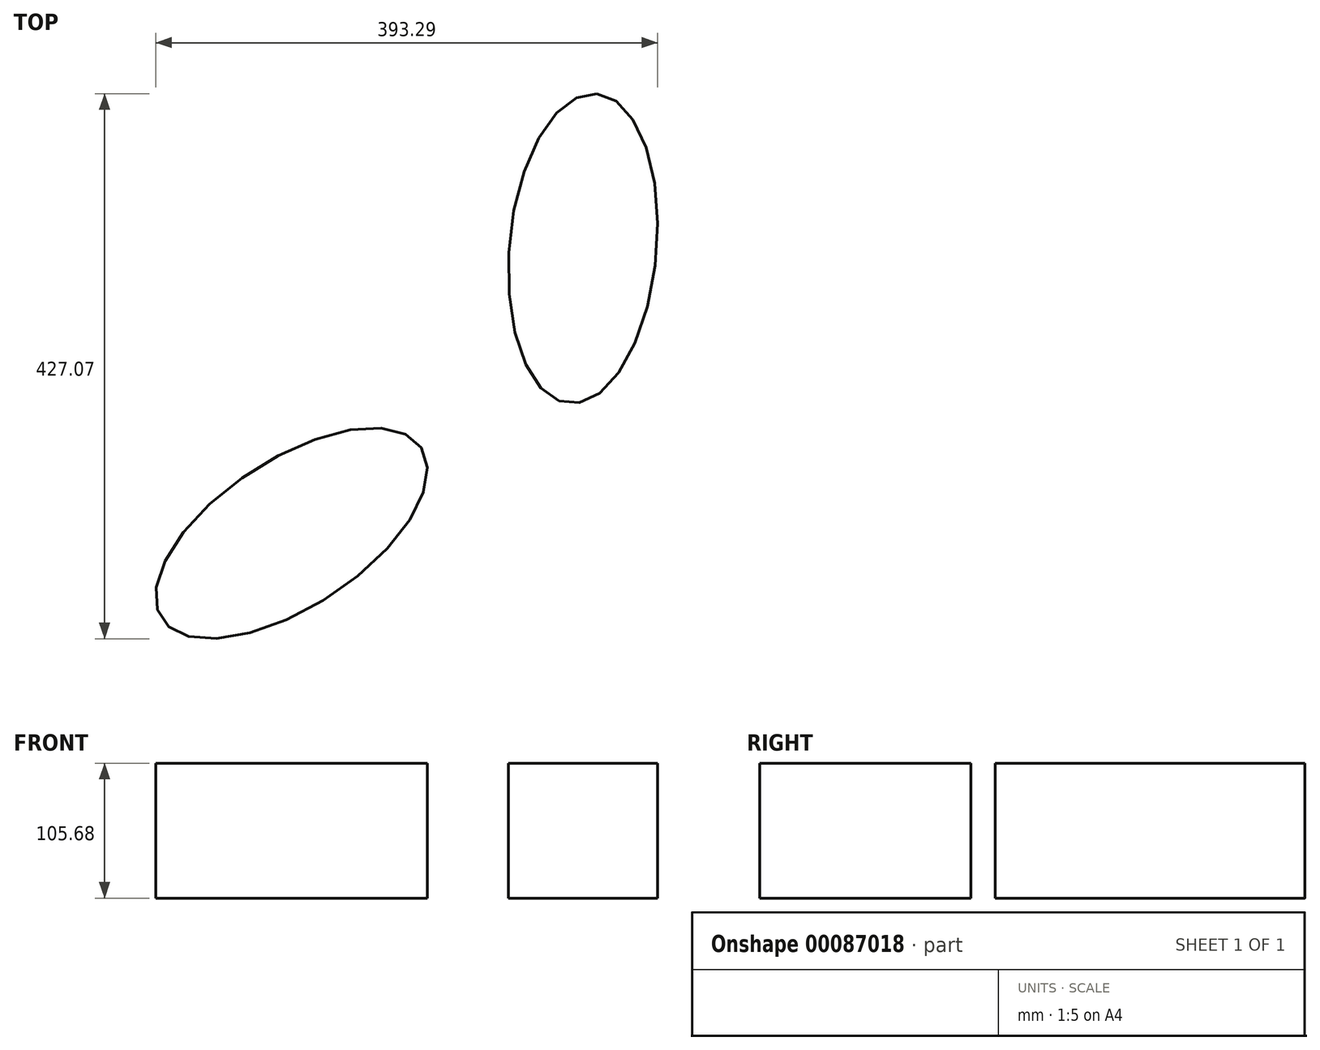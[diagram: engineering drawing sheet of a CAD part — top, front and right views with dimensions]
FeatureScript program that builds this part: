
annotation { "Feature Type Name" : "Feature", "Feature Type Description" : "" }
export const myFeature = defineFeature(function(context is Context, id is Id, definition is map)
    precondition{}
    {
        {
            var Q0;
            Q0=qCreatedBy(makeId("Top.planeOp"),FACE);
            var sketch = newSketch(context, id + "F0", { "sketchPlane" : qUnion([Q0])});
            skCircle(sketch, "E0", {"center": v(73.46, 0) * mm, "radius": 35.32 * mm});
            skCircle(sketch, "E1", {"center": v(73.46, -114.86) * mm, "radius": 11.3 * mm});
            skLineSegment(sketch, "E2", {"start": v(-153.3, -43.25) * mm, "end": v(-117, 51.28) * mm});
            skLineSegment(sketch, "E3", {"start": v(-117, 51.28) * mm, "end": v(-90.27, -12.71) * mm});
            skLineSegment(sketch, "E4", {"start": v(-90.27, -12.71) * mm, "end": v(-133.06, -53.37) * mm});
            skLineSegment(sketch, "E5", {"start": v(-182.15, -7.77) * mm, "end": v(-133.06, 50.56) * mm});
            skLineSegment(sketch, "E6.top", {"start": v(-54.52, 0) * mm, "end": v(73.46, 0) * mm});
            skLineSegment(sketch, "E6.left", {"start": v(-54.52, 24.2) * mm, "end": v(-54.52, 0) * mm});
            skLineSegment(sketch, "E7.bottom", {"start": v(131.67, -31.4) * mm, "end": v(153.76, -31.4) * mm});
            skLineSegment(sketch, "E7.top", {"start": v(131.67, -11.06) * mm, "end": v(153.76, -11.06) * mm});
            skLineSegment(sketch, "E7.left", {"start": v(131.67, -31.4) * mm, "end": v(131.67, -11.06) * mm});
            skLineSegment(sketch, "E7.right", {"start": v(153.76, -31.4) * mm, "end": v(153.76, -11.06) * mm});
            skEllipse(sketch, "E8", {"center": v(-15.34, 67.77) * mm, "majorRadius": 6.88 * mm, "minorRadius": 95.43 * mm, "majorAxis": v(-0.66, -0.75)});
            skArc(sketch, "E9", {"start": v(-139.46, -67.7) * mm, "mid": v(-100.06, -76.7) * mm, "end": v(-133.06, -53.37) * mm});
            skFitSpline(sketch, "E10", {"points": [v(101.11, -98.73) * mm, v(222.96, -90.1) * mm, v(188, -20.78) * mm, v(254.86, 0) * mm, v(125.27, 113.69) * mm, v(92, 99.58) * mm], "startDerivative": vector(706.16, -108.12) * mm, "endDerivative": vector(-179.65, -192.92) * mm, "construction": true});
            skFitSpline(sketch, "E11.0", {"points": [v(104.25, -44.37) * mm, v(108.35, -40.06) * mm, v(112.06, -35.4) * mm, v(115.31, -30.53) * mm, v(118.06, -25.54) * mm, v(120.3, -20.56) * mm, v(122.06, -15.7) * mm, v(123.38, -11) * mm, v(124.3, -6.56) * mm, v(125.1, -1) * mm, v(125.42, 5.23) * mm, v(125.13, 11.56) * mm, v(124.44, 16.87) * mm, v(123.54, 21.34) * mm, v(122.55, 25.12) * mm, v(121.52, 28.34) * mm, v(120.51, 31.11) * mm, v(119.2, 34.32) * mm, v(117.66, 37.58) * mm, v(116, 40.72) * mm, v(114.47, 43.32) * mm, v(113.08, 45.53) * mm, v(111.79, 47.47) * mm, v(110.16, 49.79) * mm, v(108.27, 52.32) * mm, v(106.1, 55.05) * mm, v(103.98, 57.61) * mm, v(101.84, 60.1) * mm, v(99.65, 62.55) * mm, v(97.4, 65.02) * mm, v(95.05, 67.53) * mm, v(92.6, 70.09) * mm, v(90.06, 72.71) * mm, v(87.4, 75.4) * mm, v(84.64, 78.17) * mm, v(81.8, 80.98) * mm, v(78.86, 83.85) * mm, v(74.83, 87.73) * mm, v(69.6, 92.71) * mm, v(63, 98.87) * mm, v(56.13, 105.17) * mm, v(50.22, 110.52) * mm, v(45.38, 114.85) * mm, v(41.71, 118.1) * mm, v(38.62, 120.83) * mm, v(36.13, 123.02) * mm, v(34.25, 124.66) * mm, v(32.37, 126.3) * mm, v(29.86, 128.46) * mm, v(26.74, 131.15) * mm, v(23.01, 134.35) * mm, v(18.07, 138.55) * mm, v(11.96, 143.68) * mm, v(4.78, 149.62) * mm, v(-2.21, 155.31) * mm, v(-7.86, 159.83) * mm, v(-12.26, 163.29) * mm, v(-15.5, 165.8) * mm, v(-18.67, 168.24) * mm, v(-21.79, 170.6) * mm, v(-24.82, 172.87) * mm, v(-27.77, 175.03) * mm, v(-30.64, 177.1) * mm, v(-33.44, 179.08) * mm, v(-36.2, 180.97) * mm, v(-38.93, 182.8) * mm, v(-41.68, 184.59) * mm, v(-44.5, 186.35) * mm, v(-47.5, 188.12) * mm, v(-50.27, 189.65) * mm, v(-52.8, 190.94) * mm, v(-54.9, 191.96) * mm, v(-57.27, 193.04) * mm, v(-60.05, 194.19) * mm, v(-63.38, 195.41) * mm, v(-66.83, 196.5) * mm, v(-70.19, 197.35) * mm, v(-73.07, 197.98) * mm, v(-76.4, 198.56) * mm, v(-80.28, 199.03) * mm, v(-84.83, 199.3) * mm, v(-90.19, 199.26) * mm, v(-96.5, 198.7) * mm, v(-102.61, 197.52) * mm, v(-108.02, 195.97) * mm, v(-112.3, 194.45) * mm, v(-116.76, 192.5) * mm, v(-121.35, 190.1) * mm, v(-125.98, 187.2) * mm, v(-130.54, 183.8) * mm, v(-134.93, 179.91) * mm, v(-139.03, 175.6) * mm, v(-142.74, 170.95) * mm, v(-146, 166.07) * mm, v(-148.74, 161.09) * mm, v(-150.98, 156.1) * mm, v(-152.74, 151.24) * mm, v(-154.06, 146.55) * mm, v(-154.98, 142.1) * mm, v(-155.78, 136.54) * mm, v(-156.1, 130.31) * mm, v(-155.81, 123.99) * mm, v(-155.12, 118.67) * mm, v(-154.22, 114.2) * mm, v(-153.23, 110.42) * mm, v(-152.2, 107.2) * mm, v(-151.2, 104.43) * mm, v(-149.88, 101.23) * mm, v(-148.34, 97.96) * mm, v(-146.67, 94.82) * mm, v(-145.15, 92.23) * mm, v(-143.76, 90.02) * mm, v(-142.47, 88.08) * mm, v(-140.84, 85.76) * mm, v(-138.95, 83.22) * mm, v(-136.78, 80.5) * mm, v(-134.66, 77.93) * mm, v(-132.52, 75.45) * mm, v(-130.33, 73) * mm, v(-128.07, 70.52) * mm, v(-125.73, 68.02) * mm, v(-123.29, 65.46) * mm, v(-120.74, 62.83) * mm, v(-118.08, 60.14) * mm, v(-115.32, 57.37) * mm, v(-112.48, 54.56) * mm, v(-109.54, 51.7) * mm, v(-105.51, 47.81) * mm, v(-100.27, 42.83) * mm, v(-93.68, 36.68) * mm, v(-86.81, 30.37) * mm, v(-80.9, 25.02) * mm, v(-76.06, 20.7) * mm, v(-72.4, 17.44) * mm, v(-69.3, 14.71) * mm, v(-66.8, 12.53) * mm, v(-64.93, 10.89) * mm, v(-63.05, 9.25) * mm, v(-60.54, 7.08) * mm, v(-57.42, 4.4) * mm, v(-53.7, 1.2) * mm, v(-48.75, -3) * mm, v(-42.64, -8.13) * mm, v(-35.46, -14.08) * mm, v(-28.47, -19.77) * mm, v(-22.82, -24.28) * mm, v(-18.42, -27.74) * mm, v(-15.18, -30.26) * mm, v(-12, -32.7) * mm, v(-8.9, -35.05) * mm, v(-5.86, -37.32) * mm, v(-2.91, -39.48) * mm, v(-0.04, -41.55) * mm, v(2.76, -43.53) * mm, v(5.51, -45.43) * mm, v(8.25, -47.26) * mm, v(11, -49.04) * mm, v(13.83, -50.8) * mm, v(16.83, -52.57) * mm, v(19.6, -54.1) * mm, v(22.11, -55.4) * mm, v(24.21, -56.42) * mm, v(26.6, -57.5) * mm, v(29.37, -58.64) * mm, v(32.7, -59.87) * mm, v(36.15, -60.95) * mm, v(39.5, -61.8) * mm, v(42.39, -62.44) * mm, v(45.72, -63.01) * mm, v(49.6, -63.48) * mm, v(54.15, -63.76) * mm, v(59.5, -63.72) * mm, v(65.81, -63.15) * mm, v(71.93, -61.98) * mm, v(77.34, -60.43) * mm, v(81.62, -58.9) * mm, v(86.08, -56.96) * mm, v(90.67, -54.56) * mm, v(95.3, -51.66) * mm, v(99.86, -48.25) * mm, v(104.25, -44.37) * mm, v(108.35, -40.06) * mm, v(112.06, -35.4) * mm, v(104.25, -44.37) * mm]});
            skEllipse(sketch, "E12", {"center": v(-365.98, -36.98) * mm, "majorRadius": 121.75 * mm, "minorRadius": 57.75 * mm, "majorAxis": v(0.35, -0.94)});
            skEllipse(sketch, "E13.1.0", {"center": v(-199.27, -309.19) * mm, "majorRadius": 121.75 * mm, "minorRadius": 57.75 * mm, "majorAxis": v(0.95, -0.3)});
            skEllipse(sketch, "E13.2.0", {"center": v(117.5, -348.57) * mm, "majorRadius": 121.75 * mm, "minorRadius": 57.75 * mm, "majorAxis": v(0.83, 0.55)});
            skEllipse(sketch, "E13.3.0", {"center": v(345.78, -125.47) * mm, "majorRadius": 121.75 * mm, "minorRadius": 57.75 * mm, "majorAxis": v(0.09, 1)});
            skEllipse(sketch, "E13.4.0", {"center": v(313.69, 192.11) * mm, "majorRadius": 121.75 * mm, "minorRadius": 57.75 * mm, "majorAxis": v(-0.72, 0.7)});
            skEllipse(sketch, "E13.5.0", {"center": v(45.38, 365.03) * mm, "majorRadius": 121.75 * mm, "minorRadius": 57.75 * mm, "majorAxis": v(-1, -0.13)});
            skEllipse(sketch, "E13.6.0", {"center": v(-257.1, 263.07) * mm, "majorRadius": 121.75 * mm, "minorRadius": 57.75 * mm, "majorAxis": v(-0.51, -0.86)});
            skPoint(sketch, "E13.center", {"position": v(0, 0) * mm});
            skSolve(sketch);
        }
        {
            var Q0;
            Q0=makeQuery(id+"F0.imprint","IMPRINT",FACE,{"disambiguationData":[TD([[makeQuery(id+"F0.imprint","IMPRINT",EDGE,{"derivedFrom":sQuery(id+"F0.wireOp",EDGE,"E13.2.0")}),1.0]])]});
            var Q1;
            Q1=makeQuery(id+"F0.imprint","IMPRINT",FACE,{"disambiguationData":[TD([[makeQuery(id+"F0.imprint","IMPRINT",EDGE,{"derivedFrom":sQuery(id+"F0.wireOp",EDGE,"E13.3.0")}),1.0]])]});
            extrude(context, id + "F1", {"entities" : qUnion([Q0, Q1]), "depth" : 105.68 * mm});
        }
    });
